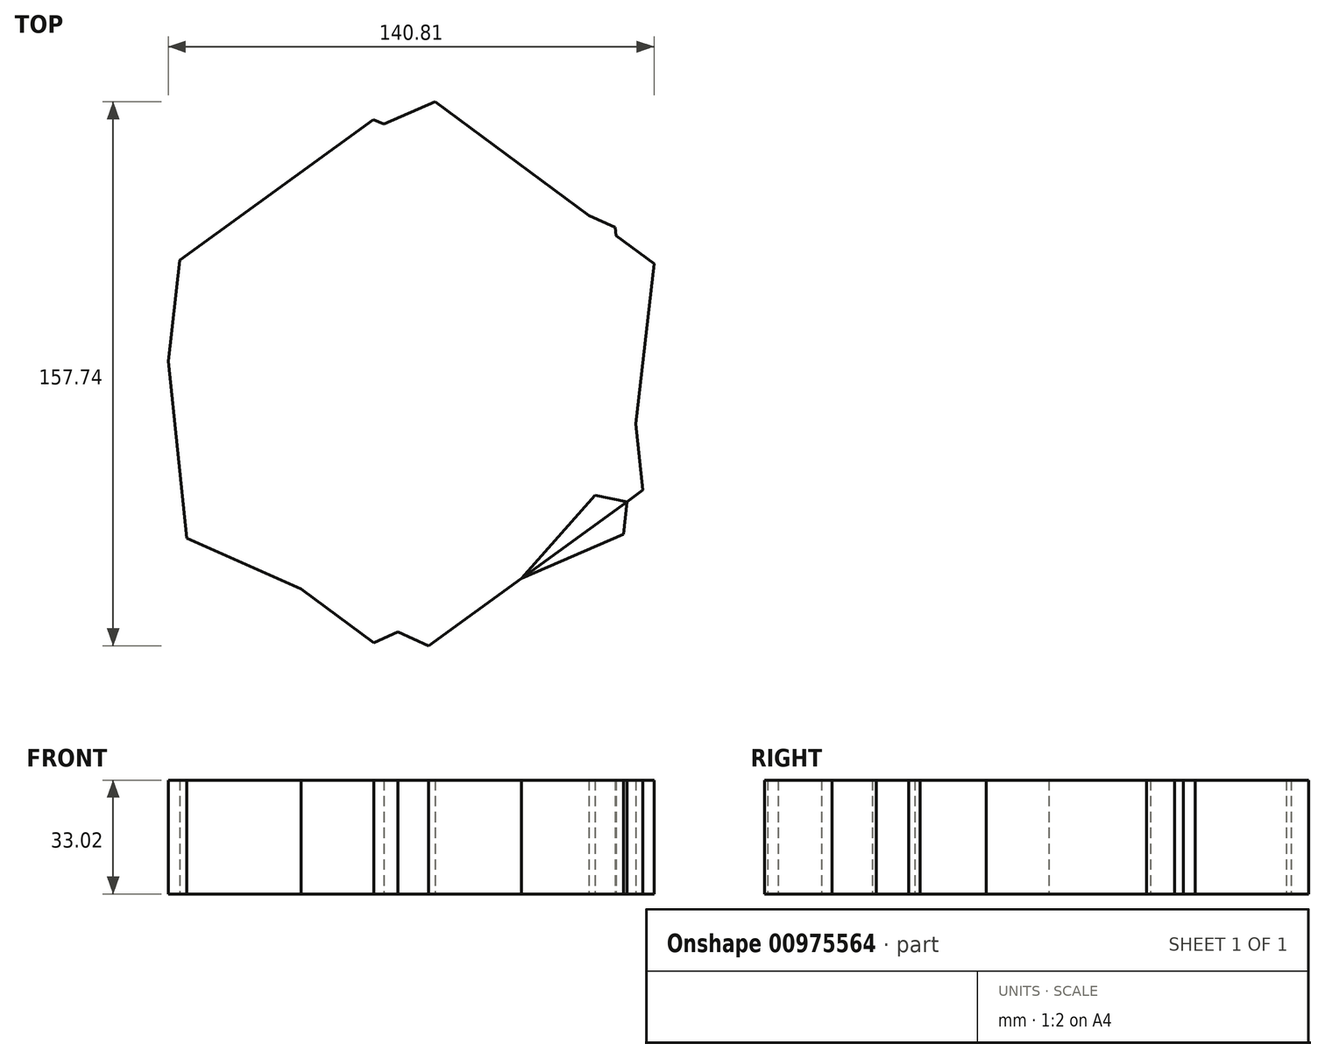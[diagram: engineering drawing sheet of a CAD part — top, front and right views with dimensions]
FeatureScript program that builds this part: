
annotation { "Feature Type Name" : "Feature", "Feature Type Description" : "" }
export const myFeature = defineFeature(function(context is Context, id is Id, definition is map)
    precondition{}
    {
        {
            var Q0;
            Q0=qCreatedBy(makeId("Top.planeOp"),FACE);
            var sketch = newSketch(context, id + "F0", { "sketchPlane" : qUnion([Q0])});
            skCircle(sketch, "E0.cCircle", {"center": v(3.16, 0) * mm, "radius": 68.36 * mm, "construction": true});
            skLineSegment(sketch, "E0.0", {"start": v(-74.18, 15.78) * mm, "end": v(-21.84, 74.87) * mm});
            skLineSegment(sketch, "E0.1", {"start": v(-21.84, 74.87) * mm, "end": v(55.5, 59.09) * mm});
            skLineSegment(sketch, "E0.2", {"start": v(55.5, 59.09) * mm, "end": v(80.5, -15.78) * mm});
            skLineSegment(sketch, "E0.3", {"start": v(80.5, -15.78) * mm, "end": v(28.17, -74.87) * mm});
            skLineSegment(sketch, "E0.4", {"start": v(28.17, -74.87) * mm, "end": v(-49.17, -59.09) * mm});
            skLineSegment(sketch, "E0.5", {"start": v(-49.17, -59.09) * mm, "end": v(-74.18, 15.78) * mm});
            skPoint(sketch, "E0.0.midPoint", {"position": v(-48, 45.32) * mm});
            skCircle(sketch, "E1.cCircle", {"center": v(0, 0) * mm, "radius": 66.45 * mm, "construction": true});
            skLineSegment(sketch, "E1.0", {"start": v(-70.1, 31.22) * mm, "end": v(-8, 76.31) * mm});
            skLineSegment(sketch, "E1.1", {"start": v(-8, 76.31) * mm, "end": v(62.08, 45.1) * mm});
            skLineSegment(sketch, "E1.2", {"start": v(62.08, 45.1) * mm, "end": v(70.1, -31.22) * mm});
            skLineSegment(sketch, "E1.3", {"start": v(70.1, -31.22) * mm, "end": v(8, -76.31) * mm});
            skLineSegment(sketch, "E1.4", {"start": v(8, -76.31) * mm, "end": v(-62.08, -45.1) * mm});
            skLineSegment(sketch, "E1.5", {"start": v(-62.08, -45.1) * mm, "end": v(-70.1, 31.22) * mm});
            skPoint(sketch, "E1.0.midPoint", {"position": v(-39.05, 53.77) * mm});
            skCircle(sketch, "E2.MirrorC", {"center": v(-77.12, 110.54) * mm, "radius": 68.36 * mm, "construction": true});
            skLineSegment(sketch, "E3.MirrorCS", {"start": v(-148.2, 138.75) * mm, "end": v(-140.18, 62.44) * mm});
            skLineSegment(sketch, "E4.MirrorCS", {"start": v(-4.75, 142.03) * mm, "end": v(-68.2, 188.96) * mm});
            skLineSegment(sketch, "E5.MirrorCS", {"start": v(-8, 76.31) * mm, "end": v(-16.02, 152.62) * mm});
            skLineSegment(sketch, "E6.MirrorCS", {"start": v(-140.18, 62.44) * mm, "end": v(-70.1, 31.22) * mm});
            skLineSegment(sketch, "E7.MirrorCS", {"start": v(-68.2, 188.96) * mm, "end": v(-140.58, 157.47) * mm});
            skLineSegment(sketch, "E8.MirrorCS", {"start": v(-16.02, 152.62) * mm, "end": v(-86.11, 183.84) * mm});
            skPoint(sketch, "E9.MirrorP", {"position": v(-49.85, 47.86) * mm});
            skLineSegment(sketch, "E10.MirrorCS", {"start": v(-13.66, 63.6) * mm, "end": v(-4.75, 142.03) * mm});
            skLineSegment(sketch, "E11.MirrorCS", {"start": v(-86.11, 183.84) * mm, "end": v(-148.2, 138.75) * mm});
            skLineSegment(sketch, "E12.MirrorCS", {"start": v(-140.58, 157.47) * mm, "end": v(-149.5, 79.05) * mm});
            skCircle(sketch, "E13.MirrorC", {"center": v(-78.1, 107.53) * mm, "radius": 66.45 * mm, "construction": true});
            skLineSegment(sketch, "E14.MirrorCS", {"start": v(-149.5, 79.05) * mm, "end": v(-86.04, 32.11) * mm});
            skLineSegment(sketch, "E15.MirrorCS", {"start": v(-86.04, 32.11) * mm, "end": v(-13.66, 63.6) * mm});
            skSolve(sketch);
        }
        {
            var Q0;
            {var subQ8=sQuery(id+"F0.wireOp",EDGE,"E0.0");var subQ19=sQuery(id+"F0.wireOp",EDGE,"E1.5");var subQ20=makeQuery(id+"F0.imprint","INTERSECT",VERTEX,{"derivedFrom":[subQ8,subQ19]});Q0=makeQuery(id+"F0.imprint","IMPRINT",FACE,{"disambiguationData":[TD([[makeQuery(id+"F0.imprint","IMPRINT",EDGE,{"disambiguationData":[TD([[subQ20,1.0]])],"derivedFrom":subQ19}),-1.0]])]});}
            var Q1;
            {var subQ6=sQuery(id+"F0.wireOp",EDGE,"E5.MirrorCS");var subQ23=sQuery(id+"F0.wireOp",EDGE,"E10.MirrorCS");var subQ24=makeQuery(id+"F0.imprint","INTERSECT",VERTEX,{"derivedFrom":[subQ6,subQ23]});Q1=makeQuery(id+"F0.imprint","IMPRINT",FACE,{"disambiguationData":[TD([[makeQuery(id+"F0.imprint","IMPRINT",EDGE,{"disambiguationData":[TD([[subQ24,-1.0]])],"derivedFrom":subQ6}),1.0]])]});}
            var Q2;
            {var subQ0=sQuery(id+"F0.wireOp",EDGE,"E4.MirrorCS");var subQ1=sQuery(id+"F0.wireOp",EDGE,"E8.MirrorCS");var subQ2=makeQuery(id+"F0.imprint","INTERSECT",VERTEX,{"derivedFrom":[subQ1,subQ0]});Q2=makeQuery(id+"F0.imprint","IMPRINT",FACE,{"disambiguationData":[TD([[makeQuery(id+"F0.imprint","IMPRINT",EDGE,{"disambiguationData":[TD([[subQ2,-1.0]])],"derivedFrom":subQ1}),-1.0]])]});}
            var Q3;
            {var subQ0=sQuery(id+"F0.wireOp",EDGE,"E0.5");var subQ1=sQuery(id+"F0.wireOp",EDGE,"E0.4");var subQ2=makeQuery(id+"F0.imprint","INTERSECT",VERTEX,{"derivedFrom":[subQ1,subQ0]});Q3=makeQuery(id+"F0.imprint","IMPRINT",FACE,{"disambiguationData":[TD([[makeQuery(id+"F0.imprint","IMPRINT",EDGE,{"disambiguationData":[TD([[subQ2,1.0]])],"derivedFrom":subQ1}),-1.0]])]});}
            var Q4;
            {var subQ0=sQuery(id+"F0.wireOp",EDGE,"E12.MirrorCS");var subQ1=sQuery(id+"F0.wireOp",EDGE,"E14.MirrorCS");var subQ2=makeQuery(id+"F0.imprint","INTERSECT",VERTEX,{"derivedFrom":[subQ1,subQ0]});Q4=makeQuery(id+"F0.imprint","IMPRINT",FACE,{"disambiguationData":[TD([[makeQuery(id+"F0.imprint","IMPRINT",EDGE,{"disambiguationData":[TD([[subQ2,-1.0]])],"derivedFrom":subQ1}),1.0]])]});}
            var Q5;
            {var subQ0=sQuery(id+"F0.wireOp",EDGE,"E0.2");var subQ1=sQuery(id+"F0.wireOp",EDGE,"E0.3");var subQ2=makeQuery(id+"F0.imprint","INTERSECT",VERTEX,{"derivedFrom":[subQ1,subQ0]});Q5=makeQuery(id+"F0.imprint","IMPRINT",FACE,{"disambiguationData":[TD([[makeQuery(id+"F0.imprint","IMPRINT",EDGE,{"disambiguationData":[TD([[subQ2,-1.0]])],"derivedFrom":subQ1}),-1.0]])]});}
            var Q6;
            {var subQ0=sQuery(id+"F0.wireOp",EDGE,"E0.3");var subQ1=sQuery(id+"F0.wireOp",EDGE,"E0.4");var subQ2=makeQuery(id+"F0.imprint","INTERSECT",VERTEX,{"derivedFrom":[subQ1,subQ0]});Q6=makeQuery(id+"F0.imprint","IMPRINT",FACE,{"disambiguationData":[TD([[makeQuery(id+"F0.imprint","IMPRINT",EDGE,{"disambiguationData":[TD([[subQ2,-1.0]])],"derivedFrom":subQ1}),-1.0]])]});}
            var Q7;
            {var subQ0=sQuery(id+"F0.wireOp",EDGE,"E3.MirrorCS");var subQ1=sQuery(id+"F0.wireOp",EDGE,"E6.MirrorCS");var subQ2=makeQuery(id+"F0.imprint","INTERSECT",VERTEX,{"derivedFrom":[subQ1,subQ0]});Q7=makeQuery(id+"F0.imprint","IMPRINT",FACE,{"disambiguationData":[TD([[makeQuery(id+"F0.imprint","IMPRINT",EDGE,{"disambiguationData":[TD([[subQ2,-1.0]])],"derivedFrom":subQ1}),1.0]])]});}
            var Q8;
            {var subQ0=sQuery(id+"F0.wireOp",EDGE,"E1.4");var subQ1=sQuery(id+"F0.wireOp",EDGE,"E1.5");var subQ2=makeQuery(id+"F0.imprint","INTERSECT",VERTEX,{"derivedFrom":[subQ1,subQ0]});Q8=makeQuery(id+"F0.imprint","IMPRINT",FACE,{"disambiguationData":[TD([[makeQuery(id+"F0.imprint","IMPRINT",EDGE,{"disambiguationData":[TD([[subQ2,-1.0]])],"derivedFrom":subQ1}),-1.0]])]});}
            var Q9;
            {var subQ0=sQuery(id+"F0.wireOp",EDGE,"E10.MirrorCS");var subQ1=sQuery(id+"F0.wireOp",EDGE,"E5.MirrorCS");var subQ2=makeQuery(id+"F0.imprint","INTERSECT",VERTEX,{"derivedFrom":[subQ1,subQ0]});Q9=makeQuery(id+"F0.imprint","IMPRINT",FACE,{"disambiguationData":[TD([[makeQuery(id+"F0.imprint","IMPRINT",EDGE,{"disambiguationData":[TD([[subQ2,-1.0]])],"derivedFrom":subQ1}),-1.0]])]});}
            var Q10;
            {var subQ0=sQuery(id+"F0.wireOp",EDGE,"E1.5");var subQ3=sQuery(id+"F0.wireOp",EDGE,"E0.0");var subQ5=makeQuery(id+"F0.imprint","INTERSECT",VERTEX,{"derivedFrom":[subQ3,subQ0]});Q10=makeQuery(id+"F0.imprint","IMPRINT",FACE,{"disambiguationData":[TD([[makeQuery(id+"F0.imprint","IMPRINT",EDGE,{"disambiguationData":[TD([[subQ5,-1.0]])],"derivedFrom":subQ3}),1.0]])]});}
            var Q11;
            {var subQ0=sQuery(id+"F0.wireOp",EDGE,"E15.MirrorCS");var subQ3=sQuery(id+"F0.wireOp",EDGE,"E10.MirrorCS");var subQ5=makeQuery(id+"F0.imprint","INTERSECT",VERTEX,{"derivedFrom":[subQ0,subQ3]});Q11=makeQuery(id+"F0.imprint","IMPRINT",FACE,{"disambiguationData":[TD([[makeQuery(id+"F0.imprint","IMPRINT",EDGE,{"disambiguationData":[TD([[subQ5,1.0]])],"derivedFrom":subQ0}),1.0]])]});}
            var Q12;
            {var subQ0=sQuery(id+"F0.wireOp",EDGE,"E7.MirrorCS");var subQ1=sQuery(id+"F0.wireOp",EDGE,"E12.MirrorCS");var subQ2=makeQuery(id+"F0.imprint","INTERSECT",VERTEX,{"derivedFrom":[subQ1,subQ0]});Q12=makeQuery(id+"F0.imprint","IMPRINT",FACE,{"disambiguationData":[TD([[makeQuery(id+"F0.imprint","IMPRINT",EDGE,{"disambiguationData":[TD([[subQ2,-1.0]])],"derivedFrom":subQ1}),1.0]])]});}
            var Q13;
            {var subQ0=sQuery(id+"F0.wireOp",EDGE,"E0.5");var subQ1=sQuery(id+"F0.wireOp",EDGE,"E0.0");var subQ2=makeQuery(id+"F0.imprint","INTERSECT",VERTEX,{"derivedFrom":[subQ1,subQ0]});Q13=makeQuery(id+"F0.imprint","IMPRINT",FACE,{"disambiguationData":[TD([[makeQuery(id+"F0.imprint","IMPRINT",EDGE,{"disambiguationData":[TD([[subQ2,-1.0]])],"derivedFrom":subQ1}),-1.0]])]});}
            var Q14;
            {var subQ0=sQuery(id+"F0.wireOp",EDGE,"E14.MirrorCS");var subQ1=sQuery(id+"F0.wireOp",EDGE,"E15.MirrorCS");var subQ2=makeQuery(id+"F0.imprint","INTERSECT",VERTEX,{"derivedFrom":[subQ1,subQ0]});Q14=makeQuery(id+"F0.imprint","IMPRINT",FACE,{"disambiguationData":[TD([[makeQuery(id+"F0.imprint","IMPRINT",EDGE,{"disambiguationData":[TD([[subQ2,-1.0]])],"derivedFrom":subQ1}),1.0]])]});}
            var Q15;
            {var subQ0=sQuery(id+"F0.wireOp",EDGE,"E0.0");var subQ3=sQuery(id+"F0.wireOp",EDGE,"E0.1");var subQ5=makeQuery(id+"F0.imprint","INTERSECT",VERTEX,{"derivedFrom":[subQ0,subQ3]});Q15=makeQuery(id+"F0.imprint","IMPRINT",FACE,{"disambiguationData":[TD([[makeQuery(id+"F0.imprint","IMPRINT",EDGE,{"disambiguationData":[TD([[subQ5,1.0]])],"derivedFrom":subQ0}),-1.0]])]});}
            var Q16;
            {var subQ0=sQuery(id+"F0.wireOp",EDGE,"E6.MirrorCS");var subQ3=sQuery(id+"F0.wireOp",EDGE,"E15.MirrorCS");var subQ5=makeQuery(id+"F0.imprint","INTERSECT",VERTEX,{"derivedFrom":[subQ3,subQ0]});Q16=makeQuery(id+"F0.imprint","IMPRINT",FACE,{"disambiguationData":[TD([[makeQuery(id+"F0.imprint","IMPRINT",EDGE,{"disambiguationData":[TD([[subQ5,-1.0]])],"derivedFrom":subQ3}),-1.0]])]});}
            var Q17;
            {var subQ0=sQuery(id+"F0.wireOp",EDGE,"E5.MirrorCS");var subQ3=sQuery(id+"F0.wireOp",EDGE,"E10.MirrorCS");var subQ5=makeQuery(id+"F0.imprint","INTERSECT",VERTEX,{"derivedFrom":[subQ0,subQ3]});Q17=makeQuery(id+"F0.imprint","IMPRINT",FACE,{"disambiguationData":[TD([[makeQuery(id+"F0.imprint","IMPRINT",EDGE,{"disambiguationData":[TD([[subQ5,1.0]])],"derivedFrom":subQ0}),1.0]])]});}
            var Q18;
            {var subQ0=sQuery(id+"F0.wireOp",EDGE,"E0.2");var subQ1=sQuery(id+"F0.wireOp",EDGE,"E0.1");var subQ2=makeQuery(id+"F0.imprint","INTERSECT",VERTEX,{"derivedFrom":[subQ1,subQ0]});Q18=makeQuery(id+"F0.imprint","IMPRINT",FACE,{"disambiguationData":[TD([[makeQuery(id+"F0.imprint","IMPRINT",EDGE,{"disambiguationData":[TD([[subQ2,1.0]])],"derivedFrom":subQ1}),-1.0]])]});}
            var Q19;
            {var subQ0=sQuery(id+"F0.wireOp",EDGE,"E1.1");var subQ3=sQuery(id+"F0.wireOp",EDGE,"E0.1");var subQ5=makeQuery(id+"F0.imprint","INTERSECT",VERTEX,{"derivedFrom":[subQ3,subQ0]});Q19=makeQuery(id+"F0.imprint","IMPRINT",FACE,{"disambiguationData":[TD([[makeQuery(id+"F0.imprint","IMPRINT",EDGE,{"disambiguationData":[TD([[subQ5,1.0]])],"derivedFrom":subQ3}),1.0]])]});}
            var Q20;
            {var subQ0=sQuery(id+"F0.wireOp",EDGE,"E1.2");var subQ1=sQuery(id+"F0.wireOp",EDGE,"E0.3");var subQ2=makeQuery(id+"F0.imprint","INTERSECT",VERTEX,{"derivedFrom":[subQ1,subQ0]});Q20=makeQuery(id+"F0.imprint","IMPRINT",FACE,{"disambiguationData":[TD([[makeQuery(id+"F0.imprint","IMPRINT",EDGE,{"disambiguationData":[TD([[subQ2,-1.0]])],"derivedFrom":subQ1}),1.0]])]});}
            var Q21;
            {var subQ0=sQuery(id+"F0.wireOp",EDGE,"E1.3");var subQ1=sQuery(id+"F0.wireOp",EDGE,"E0.4");var subQ2=makeQuery(id+"F0.imprint","INTERSECT",VERTEX,{"derivedFrom":[subQ1,subQ0]});Q21=makeQuery(id+"F0.imprint","IMPRINT",FACE,{"disambiguationData":[TD([[makeQuery(id+"F0.imprint","IMPRINT",EDGE,{"disambiguationData":[TD([[subQ2,-1.0]])],"derivedFrom":subQ1}),1.0]])]});}
            var Q22;
            {var subQ0=sQuery(id+"F0.wireOp",EDGE,"E11.MirrorCS");var subQ1=sQuery(id+"F0.wireOp",EDGE,"E12.MirrorCS");var subQ2=makeQuery(id+"F0.imprint","INTERSECT",VERTEX,{"derivedFrom":[subQ1,subQ0]});Q22=makeQuery(id+"F0.imprint","IMPRINT",FACE,{"disambiguationData":[TD([[makeQuery(id+"F0.imprint","IMPRINT",EDGE,{"disambiguationData":[TD([[subQ2,-1.0]])],"derivedFrom":subQ1}),-1.0]])]});}
            var Q23;
            {var subQ0=sQuery(id+"F0.wireOp",EDGE,"E11.MirrorCS");var subQ1=sQuery(id+"F0.wireOp",EDGE,"E8.MirrorCS");var subQ2=makeQuery(id+"F0.imprint","INTERSECT",VERTEX,{"derivedFrom":[subQ1,subQ0]});Q23=makeQuery(id+"F0.imprint","IMPRINT",FACE,{"disambiguationData":[TD([[makeQuery(id+"F0.imprint","IMPRINT",EDGE,{"disambiguationData":[TD([[subQ2,1.0]])],"derivedFrom":subQ1}),1.0]])]});}
            var Q24;
            {var subQ0=sQuery(id+"F0.wireOp",EDGE,"E8.MirrorCS");var subQ1=sQuery(id+"F0.wireOp",EDGE,"E5.MirrorCS");var subQ2=makeQuery(id+"F0.imprint","INTERSECT",VERTEX,{"derivedFrom":[subQ1,subQ0]});Q24=makeQuery(id+"F0.imprint","IMPRINT",FACE,{"disambiguationData":[TD([[makeQuery(id+"F0.imprint","IMPRINT",EDGE,{"disambiguationData":[TD([[subQ2,1.0]])],"derivedFrom":subQ1}),1.0]])]});}
            extrude(context, id + "F1", {"entities" : qUnion([Q0, Q1, Q2, Q3, Q4, Q5, Q6, Q7, Q8, Q9, Q10, Q11, Q12, Q13, Q14, Q15, Q16, Q17, Q18, Q19, Q20, Q21, Q22, Q23, Q24]), "endBound" : BoundingType.SYMMETRIC, "depth" : 33.02 * mm, "offsetDistance" : 25.4 * mm});
        }
    });
